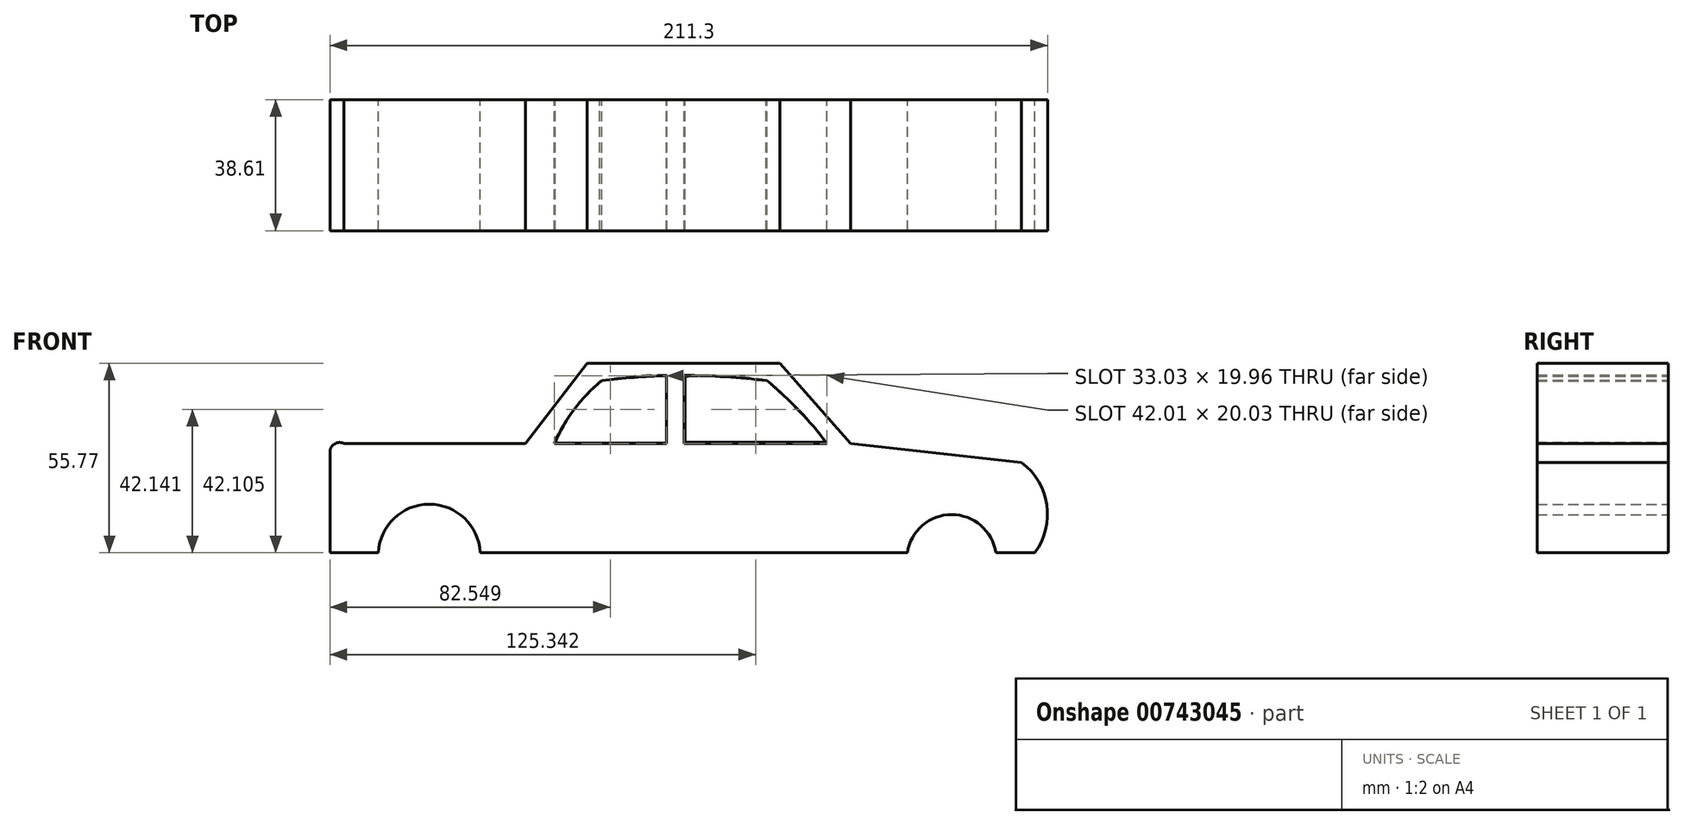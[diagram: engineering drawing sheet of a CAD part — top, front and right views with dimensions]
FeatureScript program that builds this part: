
annotation { "Feature Type Name" : "Feature", "Feature Type Description" : "" }
export const myFeature = defineFeature(function(context is Context, id is Id, definition is map)
    precondition{}
    {
        {
            var Q0;
            Q0=qCreatedBy(makeId("Front.planeOp"),FACE);
            var sketch = newSketch(context, id + "F0", { "sketchPlane" : qUnion([Q0])});
            skLineSegment(sketch, "E0", {"start": v(-12.73, 5.6) * mm, "end": v(5.46, 29.25) * mm});
            skLineSegment(sketch, "E1", {"start": v(5.46, 29.25) * mm, "end": v(62.13, 29.25) * mm});
            skLineSegment(sketch, "E2", {"start": v(62.13, 29.25) * mm, "end": v(83.04, 5.6) * mm});
            skLineSegment(sketch, "E3", {"start": v(83.04, 5.6) * mm, "end": v(133.35, 0) * mm});
            skArc(sketch, "E4", {"start": v(137.29, -26.52) * mm, "mid": v(140.79, -12.45) * mm, "end": v(133.35, 0) * mm});
            skLineSegment(sketch, "E5", {"start": v(137.29, -26.52) * mm, "end": v(125.77, -26.52) * mm});
            skLineSegment(sketch, "E6", {"start": v(-70.31, -26.52) * mm, "end": v(-56.07, -26.52) * mm});
            skLineSegment(sketch, "E7", {"start": v(-26.06, -26.52) * mm, "end": v(99.7, -26.52) * mm});
            skArc(sketch, "E8", {"start": v(76.04, 5.6) * mm, "mid": v(67.77, 15.38) * mm, "end": v(58.39, 24.1) * mm});
            skArc(sketch, "E9", {"start": v(58.39, 24.1) * mm, "mid": v(46.23, 25.25) * mm, "end": v(34.03, 25.63) * mm});
            skArc(sketch, "E10", {"start": v(9.67, 24.1) * mm, "mid": v(1.6, 15.68) * mm, "end": v(-4.28, 5.6) * mm});
            skLineSegment(sketch, "E11", {"start": v(-4.28, 5.6) * mm, "end": v(28.76, 5.6) * mm});
            skLineSegment(sketch, "E12", {"start": v(34.03, 25.63) * mm, "end": v(34.03, 5.6) * mm});
            skLineSegment(sketch, "E13", {"start": v(28.76, 25.56) * mm, "end": v(28.76, 5.6) * mm});
            skArc(sketch, "E14.trimOffspring", {"start": v(28.76, 25.56) * mm, "mid": v(19.2, 25.07) * mm, "end": v(9.67, 24.1) * mm});
            skLineSegment(sketch, "E15.trimOffspring", {"start": v(34.03, 5.6) * mm, "end": v(76.04, 5.6) * mm});
            skArc(sketch, "E16", {"start": v(125.77, -26.52) * mm, "mid": v(112.74, -15.32) * mm, "end": v(99.7, -26.52) * mm});
            skArc(sketch, "E17", {"start": v(-26.06, -26.52) * mm, "mid": v(-41.07, -12.25) * mm, "end": v(-56.07, -26.52) * mm});
            skLineSegment(sketch, "E18", {"start": v(-12.73, 5.6) * mm, "end": v(-66.17, 5.6) * mm});
            skLineSegment(sketch, "E19", {"start": v(-70.31, -26.52) * mm, "end": v(-70.31, 3.08) * mm});
            skArc(sketch, "E20", {"start": v(-66.17, 5.6) * mm, "mid": v(-68.95, 5.5) * mm, "end": v(-70.31, 3.08) * mm});
            skSolve(sketch);
        }
        {
            var Q0;
            Q0 = qSketchRegion(id + "F0", true);
            extrude(context, id + "F1", {"entities" : qUnion([Q0]), "depth" : 38.6 * mm, "offsetDistance" : 25.4 * mm});
        }
        {
            var Q0;
            Q0=qCreatedBy(makeId("Front.planeOp"),FACE);
            var sketch = newSketch(context, id + "F2", { "sketchPlane" : qUnion([Q0])});
            skArc(sketch, "E21", {"start": v(75.99, 5.94) * mm, "mid": v(67.53, 15.58) * mm, "end": v(58.15, 24.32) * mm});
            skLineSegment(sketch, "E22", {"start": v(75.99, 5.94) * mm, "end": v(34.18, 5.94) * mm});
            skLineSegment(sketch, "E23", {"start": v(34.18, 5.94) * mm, "end": v(34.18, 25.4) * mm});
            skArc(sketch, "E24", {"start": v(58.15, 24.32) * mm, "mid": v(46.2, 25.52) * mm, "end": v(34.18, 25.4) * mm});
            skLineSegment(sketch, "E25", {"start": v(28.96, 25.77) * mm, "end": v(28.96, 5.76) * mm});
            skLineSegment(sketch, "E26", {"start": v(28.96, 5.76) * mm, "end": v(-4.02, 5.76) * mm});
            skArc(sketch, "E27", {"start": v(28.96, 25.77) * mm, "mid": v(18.99, 25.47) * mm, "end": v(9.13, 23.96) * mm});
            skArc(sketch, "E28", {"start": v(9.13, 23.96) * mm, "mid": v(1.5, 15.62) * mm, "end": v(-4.02, 5.76) * mm});
            skSolve(sketch);
        }
        {
            var Q0;
            Q0 = qSketchRegion(id + "F2", true);
            extrude(context, id + "F3", {"entities" : qUnion([Q0]), "depth" : 38.6 * mm, "offsetDistance" : 25.4 * mm});
        }
    });
